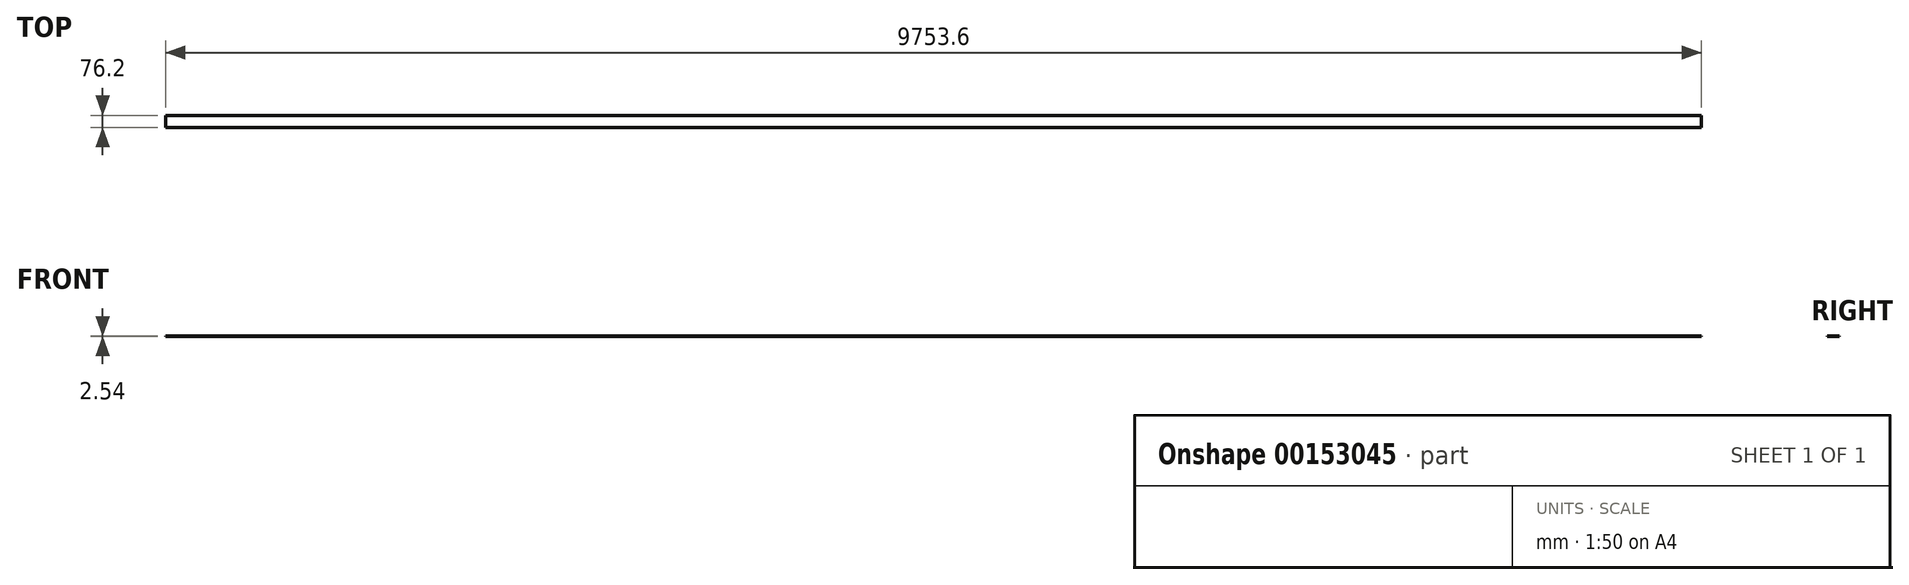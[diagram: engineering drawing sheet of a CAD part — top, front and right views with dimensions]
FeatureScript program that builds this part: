
annotation { "Feature Type Name" : "Feature", "Feature Type Description" : "" }
export const myFeature = defineFeature(function(context is Context, id is Id, definition is map)
    precondition{}
    {
        {
            var Q0;
            Q0=qCreatedBy(makeId("Top.planeOp"),FACE);
            var sketch = newSketch(context, id + "F0", { "sketchPlane" : qUnion([Q0])});
            skLineSegment(sketch, "E0.bottom", {"start": v(-210.3, 40.41) * mm, "end": v(9543.3, 40.41) * mm});
            skLineSegment(sketch, "E0.top", {"start": v(-210.3, -35.79) * mm, "end": v(9543.3, -35.79) * mm});
            skLineSegment(sketch, "E0.left", {"start": v(-210.3, 40.41) * mm, "end": v(-210.3, -35.79) * mm});
            skLineSegment(sketch, "E0.right", {"start": v(9543.3, 40.41) * mm, "end": v(9543.3, -35.79) * mm});
            skSolve(sketch);
        }
        {
            var Q0;
            Q0 = qSketchRegion(id + "F0", true);
            extrude(context, id + "F1", {"entities" : qUnion([Q0]), "depth" : 2.54 * mm});
        }
    });
